SOLIDWORKS PART (.sldprt)
format: sldprt  version: not decoded by parser v0  size: 171,520 bytes
history: native  units: mm
features: sketch x7, thread x4, hole x2, material x1, extrude x1, cut_extrude x1 (+11 scaffold rows collapsed)
feature tree (27):
  scaffold x11  (default folders/planes/origin — collapsed)
  material  "Material <not specified>"
  sketch  "Sketch1"  dims[D1=22.5mm]
  extrude  "Boss-Extrude1"  Depth=40mm
  sketch  "Sketch2"  dims[D1=5.0mm D2=10.0mm]
  cut_extrude  "Cut-Extrude1"  Depth=40mm
  sketch  "Sketch3"
  hole  "M3x0.5 Tapped Hole2"  Diameter=2.5mm Depth=6.5mm
  sketch  "Sketch6"  dims[D1=10.0mm D2=10.0mm]
  sketch  "Sketch5"  dims[hole-wizard template sketch: 47 standard entries collapsed; hole parameters kept: c15.Tap Drill Depth=6.5mm c15.D3=~14.816244mm c15.Drill Angle=118.0deg]
  thread  "Hole Thread3"  Diameter=4mm  [1 undecoded]
  thread  "Hole Thread4"  Diameter=4mm  [1 undecoded]
  hole  "M3x0.5 Tapped Hole3"  Diameter=2.5mm Depth=6.5mm
  sketch  "Sketch8"
  sketch  "Sketch7"  dims[hole-wizard template sketch: 47 standard entries collapsed; hole parameters kept: c15.Tap Drill Depth=6.5mm c15.D3=~14.816244mm c15.Drill Angle=118.0deg]
  thread  "Hole Thread5"  Diameter=4mm  [1 undecoded]
  thread  "Hole Thread6"  Diameter=4mm  [1 undecoded]
decode coverage: 13 of 15 modeling features carry decoded parameters
note: ~ marks probable driven/reference dimensions
note: 4 parameter values undecoded
note: suppression state not decoded; provenance and decode notes live in map.json
